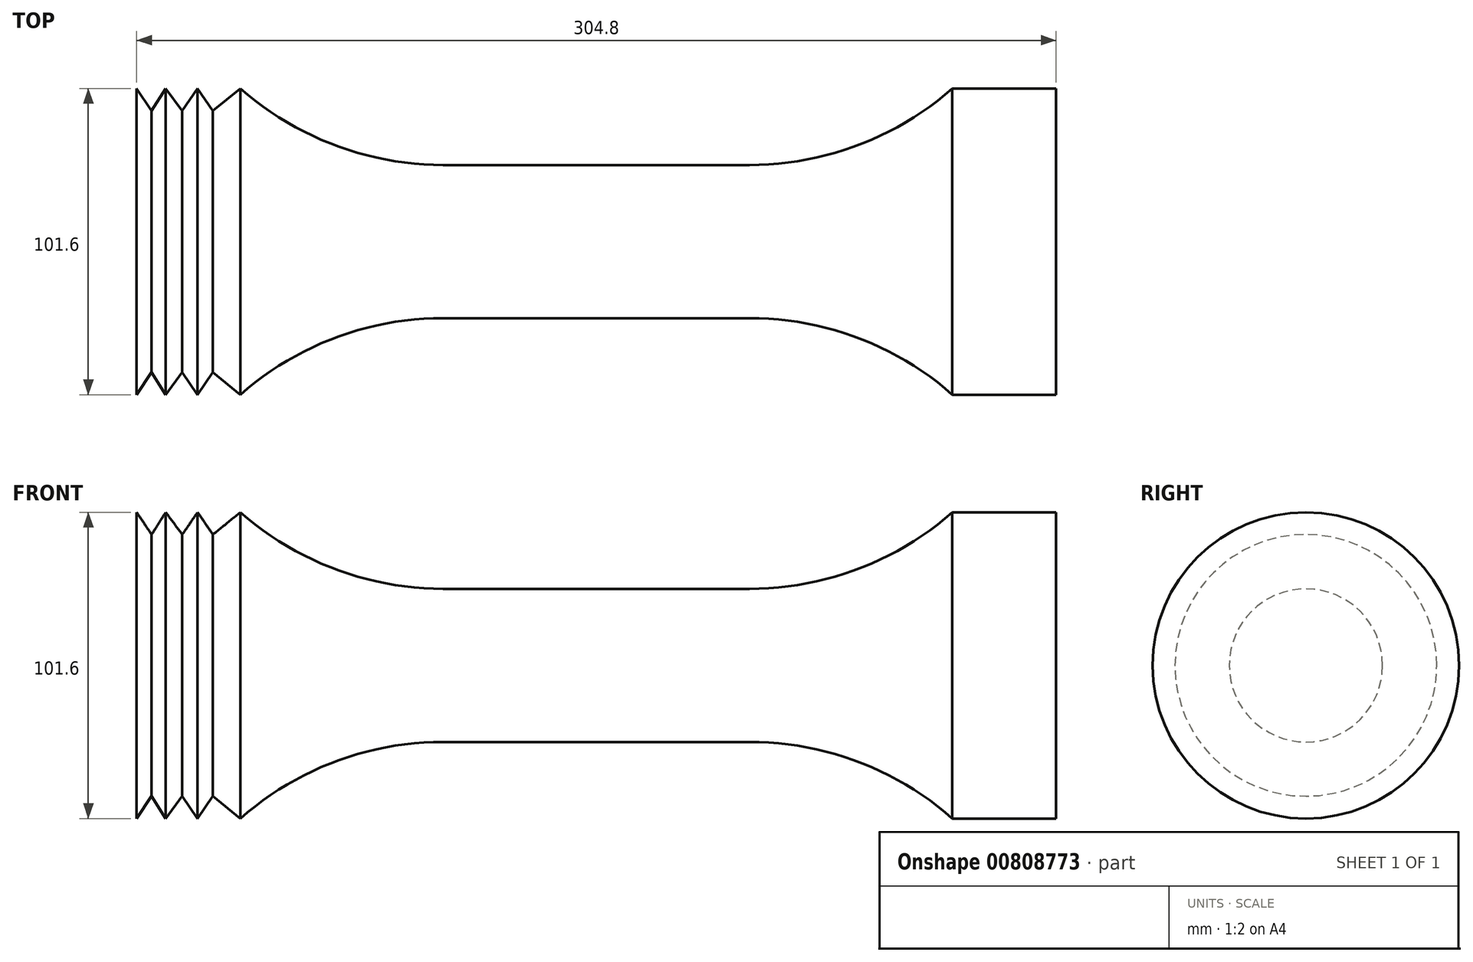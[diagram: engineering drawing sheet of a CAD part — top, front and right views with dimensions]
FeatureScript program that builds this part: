
annotation { "Feature Type Name" : "Feature", "Feature Type Description" : "" }
export const myFeature = defineFeature(function(context is Context, id is Id, definition is map)
    precondition{}
    {
        {
            var Q0;
            Q0=qCreatedBy(makeId("Front.planeOp"),FACE);
            var sketch = newSketch(context, id + "F0", { "sketchPlane" : qUnion([Q0])});
            skLineSegment(sketch, "E0", {"start": v(-77.67, 0) * mm, "end": v(227.13, 0) * mm});
            skLineSegment(sketch, "E1", {"start": v(227.13, 0) * mm, "end": v(227.13, 50.8) * mm});
            skLineSegment(sketch, "E2", {"start": v(-77.67, 50.8) * mm, "end": v(-77.67, 0) * mm});
            skLineSegment(sketch, "E3", {"start": v(23.93, 25.4) * mm, "end": v(125.53, 25.4) * mm});
            skArc(sketch, "E4", {"start": v(125.53, 25.4) * mm, "mid": v(161.45, 31.96) * mm, "end": v(192.73, 50.8) * mm});
            skArc(sketch, "E5", {"start": v(-43.27, 50.8) * mm, "mid": v(-12, 31.96) * mm, "end": v(23.93, 25.4) * mm});
            skLineSegment(sketch, "E6", {"start": v(-77.67, 50.8) * mm, "end": v(-72.7, 43.4) * mm});
            skLineSegment(sketch, "E7", {"start": v(-72.7, 43.4) * mm, "end": v(-68.04, 50.8) * mm});
            skLineSegment(sketch, "E8", {"start": v(-68.04, 50.8) * mm, "end": v(-62.54, 43.4) * mm});
            skLineSegment(sketch, "E9", {"start": v(-62.54, 43.4) * mm, "end": v(-57.46, 50.8) * mm});
            skLineSegment(sketch, "E10", {"start": v(-57.46, 50.8) * mm, "end": v(-52.39, 43.4) * mm});
            skLineSegment(sketch, "E11", {"start": v(-52.39, 43.4) * mm, "end": v(-43.27, 50.8) * mm});
            skLineSegment(sketch, "E12", {"start": v(192.73, 50.8) * mm, "end": v(227.13, 50.8) * mm});
            skSolve(sketch);
        }
        {
            var Q0;
            Q0=makeQuery(id+"F0.imprint","IMPRINT",FACE,{"disambiguationData":[TD([[makeQuery(id+"F0.imprint","IMPRINT",EDGE,{"derivedFrom":sQuery(id+"F0.wireOp",EDGE,"E0")}),1.0]])]});
            var Q1;
            Q1=sQuery(id+"F0.wireOp",EDGE,"E0");
            revolve(context, id + "F1", {"surfaceOperationType" : NewSurfaceOperationType.NEW, "entities" : qUnion([Q0]), "axis" : qUnion([Q1]), "revolveType" : RevolveType.FULL});
        }
    });
